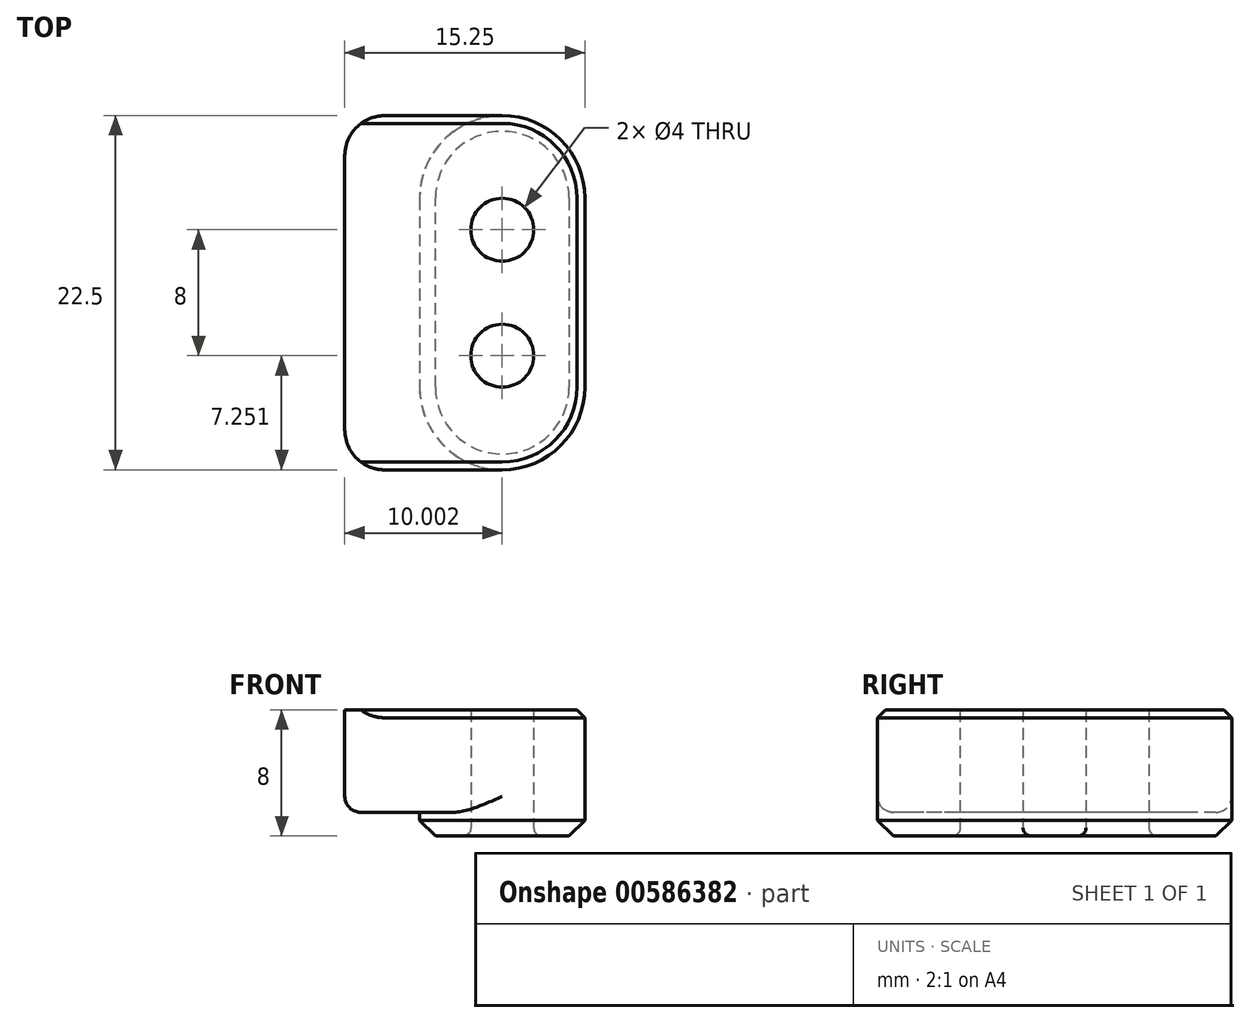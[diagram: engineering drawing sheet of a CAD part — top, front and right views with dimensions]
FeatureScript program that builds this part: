
annotation { "Feature Type Name" : "Feature", "Feature Type Description" : "" }
export const myFeature = defineFeature(function(context is Context, id is Id, definition is map)
    precondition{}
    {
        {
            var Q0;
            Q0=qCreatedBy(makeId("Top.planeOp"),FACE);
            var sketch = newSketch(context, id + "F0", { "sketchPlane" : qUnion([Q0])});
            skLineSegment(sketch, "E0.left", {"start": v(27.87, 6.45) * mm, "end": v(27.87, -5.55) * mm});
            skLineSegment(sketch, "E0.right", {"start": v(38.37, 6.45) * mm, "end": v(38.37, -5.55) * mm});
            skArc(sketch, "E1", {"start": v(38.37, 6.45) * mm, "mid": v(33.12, 11.7) * mm, "end": v(27.87, 6.45) * mm});
            skArc(sketch, "E2", {"start": v(27.87, -5.55) * mm, "mid": v(33.12, -10.8) * mm, "end": v(38.37, -5.55) * mm});
            skPoint(sketch, "E3.startSnap0", {"position": v(38.37, 0.45) * mm});
            skCircle(sketch, "E4", {"center": v(33.12, 4.45) * mm, "radius": 2 * mm});
            skCircle(sketch, "E5", {"center": v(33.12, -3.55) * mm, "radius": 2 * mm});
            skPoint(sketch, "E6.orphan", {"position": v(33.12, 0.45) * mm});
            skSolve(sketch);
        }
        {
            var Q0;
            Q0 = qSketchRegion(id + "F0", true);
            extrude(context, id + "F1", {"entities" : qUnion([Q0]), "depth" : 1.5 * mm, "offsetDistance" : 25.4 * mm});
        }
        {
            var Q0;
            Q0=makeQuery(id+"F1.opExtrude","CAP_FACE",FACE,{"disambiguationData":[OSD([sQuery(id+"F0.wireOp",EDGE,"E0.left"),sQuery(id+"F0.wireOp",EDGE,"E0.right"),sQuery(id+"F0.wireOp",EDGE,"E1"),sQuery(id+"F0.wireOp",EDGE,"E2"),sQuery(id+"F0.wireOp",EDGE,"E4"),sQuery(id+"F0.wireOp",EDGE,"E5")])],"isStart":false});
            var sketch = newSketch(context, id + "F2", { "sketchPlane" : qUnion([Q0])});
            skArc(sketch, "E7.0", {"start": v(38.37, 6.45) * mm, "mid": v(36.83, 10.16) * mm, "end": v(33.12, 11.7) * mm});
            skArc(sketch, "E8.0", {"start": v(33.12, -10.8) * mm, "mid": v(36.83, -9.26) * mm, "end": v(38.37, -5.55) * mm});
            skPoint(sketch, "E9.orphan", {"position": v(27.87, 6.45) * mm});
            skPoint(sketch, "E10.orphan", {"position": v(27.87, -5.55) * mm});
            skLineSegment(sketch, "E11", {"start": v(38.37, 6.45) * mm, "end": v(38.37, -5.55) * mm});
            skLineSegment(sketch, "E12.bottom", {"start": v(33.12, 11.7) * mm, "end": v(23.12, 11.7) * mm});
            skLineSegment(sketch, "E12.top", {"start": v(33.12, -10.8) * mm, "end": v(23.12, -10.8) * mm});
            skLineSegment(sketch, "E12.right", {"start": v(23.12, 11.7) * mm, "end": v(23.12, -10.8) * mm});
            skCircle(sketch, "E13.0", {"center": v(33.12, 4.45) * mm, "radius": 2 * mm});
            skCircle(sketch, "E14.0", {"center": v(33.12, -3.55) * mm, "radius": 2 * mm});
            skSolve(sketch);
        }
        {
            var Q0;
            Q0 = qSketchRegion(id + "F2", true);
            extrude(context, id + "F3", {"entities" : qUnion([Q0]), "operationType" : NewBodyOperationType.ADD, "depth" : 6.5 * mm, "offsetDistance" : 25.4 * mm});
        }
        {
            var Q0;
            Q0=makeQuery(id+"F1.opExtrude","CAP_EDGE",EDGE,{"disambiguationData":[OSD([sQuery(id+"F0.wireOp",EDGE,"E0.left")])],"isStart":true});
            chamfer(context, id + "F4", {"entities" : qUnion([Q0]), "width" : 1 * mm, "tangentPropagation" : true});
        }
        {
            var Q0;
            Q0=makeQuery(id+"F3.opExtrude","CAP_EDGE",EDGE,{"disambiguationData":[OSD([sQuery(id+"F2.wireOp",EDGE,"E12.bottom")])],"isStart":true});
            var Q1;
            Q1=makeQuery(id+"F3.opExtrude","CAP_EDGE",EDGE,{"disambiguationData":[OSD([sQuery(id+"F2.wireOp",EDGE,"E12.right")])],"isStart":true});
            var Q2;
            Q2=makeQuery(id+"F3.opExtrude","CAP_EDGE",EDGE,{"disambiguationData":[OSD([sQuery(id+"F2.wireOp",EDGE,"E12.top")])],"isStart":true});
            fillet(context, id + "F5", {"entities" : qUnion([Q0, Q1, Q2]), "radius" : 1 * mm, "tangentPropagation" : true, "allowEdgeOverflow" : false});
        }
        {
            var Q0;
            Q0=makeQuery(id+"F3.opExtrude","CAP_EDGE",EDGE,{"disambiguationData":[OSD([sQuery(id+"F2.wireOp",EDGE,"E12.bottom")])],"isStart":false});
            chamfer(context, id + "F6", {"entities" : qUnion([Q0]), "width" : 0.5 * mm, "tangentPropagation" : true});
        }
        {
            var Q0;
            Q0=makeQuery(id+"F1.opExtrude","CAP_EDGE",EDGE,{"disambiguationData":[OSD([sQuery(id+"F0.wireOp",EDGE,"E5")])],"isStart":true});
            var Q1;
            Q1=makeQuery(id+"F1.opExtrude","CAP_EDGE",EDGE,{"disambiguationData":[OSD([sQuery(id+"F0.wireOp",EDGE,"E4")])],"isStart":true});
            fillet(context, id + "F7", {"entities" : qUnion([Q0, Q1]), "radius" : 0.5 * mm, "tangentPropagation" : true, "allowEdgeOverflow" : false});
        }
        {
            var Q0;
            Q0=makeQuery(id+"F3.opExtrude","SWEPT_EDGE",EDGE,{"disambiguationData":[OSD([sQuery(id+"F2.wireOp",EDGE,"E12.bottom"),sQuery(id+"F2.wireOp",EDGE,"E12.right")])]});
            var Q1;
            Q1=makeQuery(id+"F3.opExtrude","SWEPT_EDGE",EDGE,{"disambiguationData":[OSD([sQuery(id+"F2.wireOp",EDGE,"E12.top"),sQuery(id+"F2.wireOp",EDGE,"E12.right")])]});
            fillet(context, id + "F8", {"entities" : qUnion([Q0, Q1]), "radius" : 2.54 * mm, "tangentPropagation" : true, "allowEdgeOverflow" : false});
        }
    });
